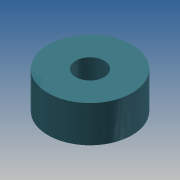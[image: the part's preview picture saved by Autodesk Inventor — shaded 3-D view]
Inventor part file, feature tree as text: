
AUTODESK INVENTOR PART (.ipt)
format: ipt  version: 2013 (Build 170138000, 138)  size: 80,384 bytes
history: native  units: mm
features: extrude x2, sketch x2
ambient origin geometry x8: Origin, YZ Plane, XZ Plane, XY Plane, X Axis, Y Axis, Z Axis, Center Point
bodies: Solid1 (feature_tree)
feature tree (4):
  extrude  "Extrusion1"  Depth=14.8mm TaperAngle=0.0deg
  extrude  "Extrusion2"  Depth=10.96mm TaperAngle=0.0deg
  sketch  "Sketch1"  dims[d0=25.0mm d2=14.8mm d3=0.0mm]
  sketch  "Sketch2"  dims[d4=8.5mm d6=10.96mm d7=0.0mm]
